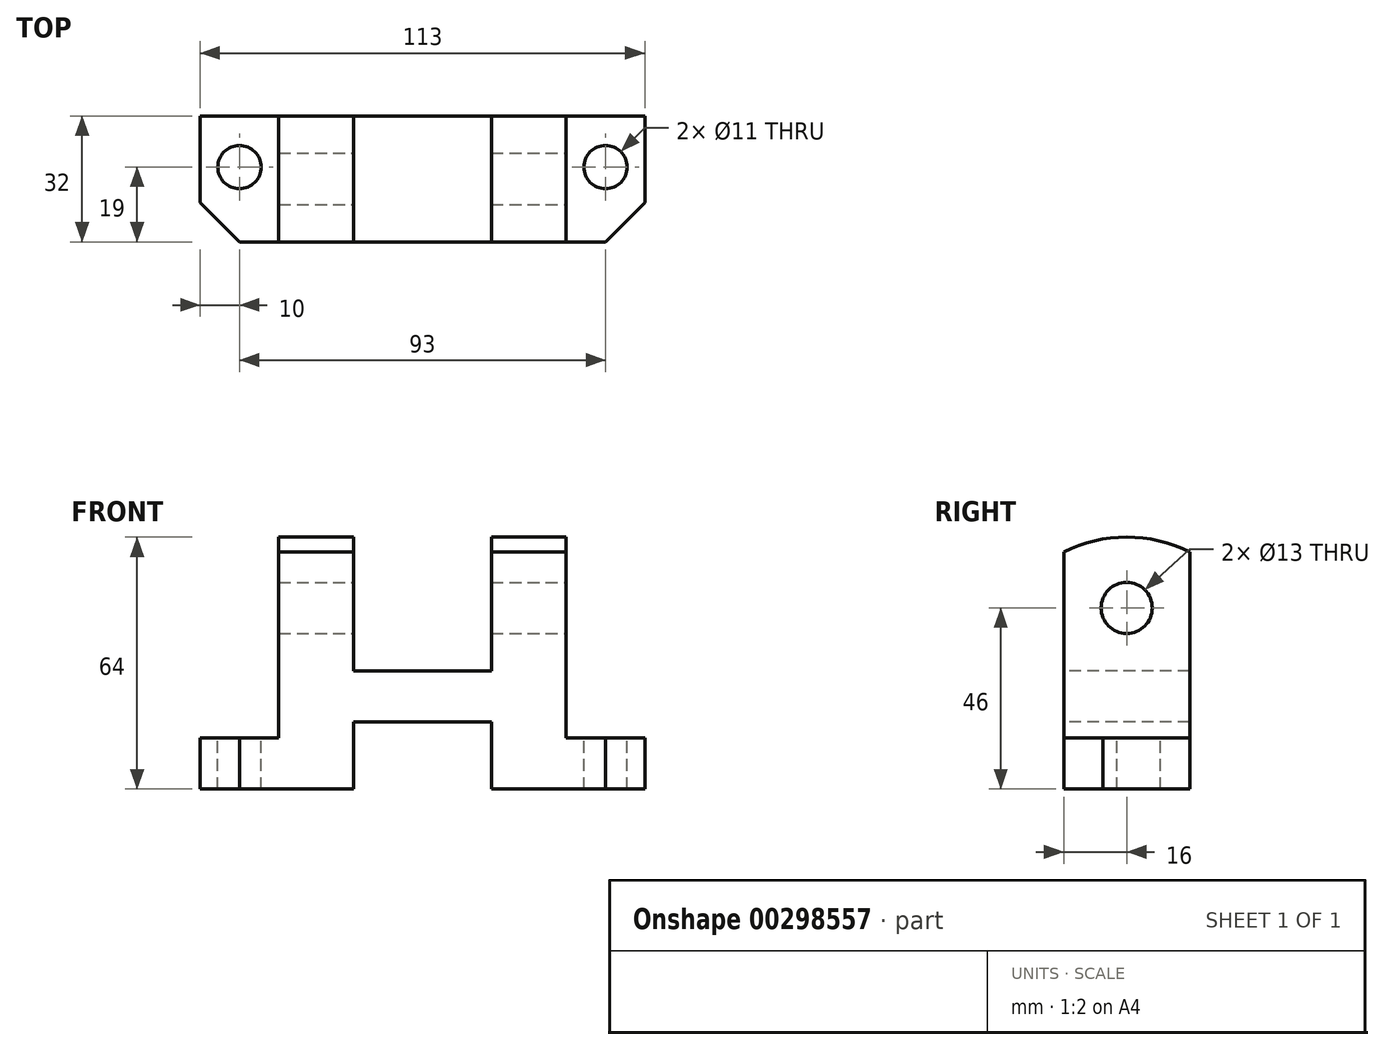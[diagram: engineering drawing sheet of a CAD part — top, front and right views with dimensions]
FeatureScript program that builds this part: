
annotation { "Feature Type Name" : "Feature", "Feature Type Description" : "" }
export const myFeature = defineFeature(function(context is Context, id is Id, definition is map)
    precondition{}
    {
        {
            var Q0;
            Q0=qCreatedBy(makeId("Front.planeOp"),FACE);
            var sketch = newSketch(context, id + "F0", { "sketchPlane" : qUnion([Q0])});
            skLineSegment(sketch, "E0.bottom", {"start": v(0, 0) * mm, "end": v(113, 0) * mm});
            skLineSegment(sketch, "E0.top", {"start": v(0, 64) * mm, "end": v(113, 64) * mm});
            skLineSegment(sketch, "E0.left", {"start": v(0, 0) * mm, "end": v(0, 64) * mm});
            skLineSegment(sketch, "E0.right", {"start": v(113, 0) * mm, "end": v(113, 64) * mm});
            skSolve(sketch);
        }
        {
            var Q0;
            Q0 = qSketchRegion(id + "F0", true);
            extrude(context, id + "F1", {"entities" : qUnion([Q0]), "depth" : 32 * mm});
        }
        {
            var Q0;
            Q0=makeQuery(id+"F1.opExtrude","CAP_FACE",FACE,{"disambiguationData":[OSD([sQuery(id+"F0.wireOp",EDGE,"E0.bottom"),sQuery(id+"F0.wireOp",EDGE,"E0.top"),sQuery(id+"F0.wireOp",EDGE,"E0.left"),sQuery(id+"F0.wireOp",EDGE,"E0.right")])],"isStart":false});
            var sketch = newSketch(context, id + "F2", { "sketchPlane" : qUnion([Q0])});
            skLineSegment(sketch, "E1.bottom", {"start": v(39, 0) * mm, "end": v(74, 0) * mm});
            skLineSegment(sketch, "E1.top", {"start": v(39, 17) * mm, "end": v(74, 17) * mm});
            skLineSegment(sketch, "E1.left", {"start": v(39, 0) * mm, "end": v(39, 17) * mm});
            skLineSegment(sketch, "E1.right", {"start": v(74, 0) * mm, "end": v(74, 17) * mm});
            skLineSegment(sketch, "E2.bottom", {"start": v(39, 64) * mm, "end": v(74, 64) * mm});
            skLineSegment(sketch, "E2.top", {"start": v(39, 30) * mm, "end": v(74, 30) * mm});
            skLineSegment(sketch, "E2.left", {"start": v(39, 64) * mm, "end": v(39, 30) * mm});
            skLineSegment(sketch, "E2.right", {"start": v(74, 64) * mm, "end": v(74, 30) * mm});
            skLineSegment(sketch, "E3.bottom", {"start": v(0, 64) * mm, "end": v(20, 64) * mm});
            skLineSegment(sketch, "E3.top", {"start": v(0, 13) * mm, "end": v(20, 13) * mm});
            skLineSegment(sketch, "E3.left", {"start": v(0, 64) * mm, "end": v(0, 13) * mm});
            skLineSegment(sketch, "E3.right", {"start": v(20, 64) * mm, "end": v(20, 13) * mm});
            skLineSegment(sketch, "E4.bottom", {"start": v(113, 64) * mm, "end": v(93, 64) * mm});
            skLineSegment(sketch, "E4.top", {"start": v(113, 13) * mm, "end": v(93, 13) * mm});
            skLineSegment(sketch, "E4.left", {"start": v(113, 64) * mm, "end": v(113, 13) * mm});
            skLineSegment(sketch, "E4.right", {"start": v(93, 64) * mm, "end": v(93, 13) * mm});
            skSolve(sketch);
        }
        {
            var Q0;
            Q0=makeQuery(id+"F2.imprint","IMPRINT",FACE,{"disambiguationData":[TD([[makeQuery(id+"F2.imprint","IMPRINT",EDGE,{"derivedFrom":sQuery(id+"F2.wireOp",EDGE,"E3.bottom")}),-1.0]])]});
            var Q1;
            Q1=makeQuery(id+"F2.imprint","IMPRINT",FACE,{"disambiguationData":[TD([[makeQuery(id+"F2.imprint","IMPRINT",EDGE,{"derivedFrom":sQuery(id+"F2.wireOp",EDGE,"E2.bottom")}),-1.0]])]});
            var Q2;
            Q2=makeQuery(id+"F2.imprint","IMPRINT",FACE,{"disambiguationData":[TD([[makeQuery(id+"F2.imprint","IMPRINT",EDGE,{"derivedFrom":sQuery(id+"F2.wireOp",EDGE,"E1.bottom")}),1.0]])]});
            var Q3;
            Q3=makeQuery(id+"F2.imprint","IMPRINT",FACE,{"disambiguationData":[TD([[makeQuery(id+"F2.imprint","IMPRINT",EDGE,{"derivedFrom":sQuery(id+"F2.wireOp",EDGE,"E4.bottom")}),-1.0]])]});
            extrude(context, id + "F3", {"entities" : qUnion([Q0, Q1, Q2, Q3]), "operationType" : NewBodyOperationType.REMOVE, "endBound" : BoundingType.THROUGH_ALL, "oppositeDirection" : true, "depth" : 25 * mm});
        }
        {
            var Q0;
            Q0=makeQuery(id+"F3.boolean.opBoolean","COPY",FACE,{"derivedFrom":makeQuery(id+"F3.opExtrude","SWEPT_FACE",FACE,{"disambiguationData":[OSD([sQuery(id+"F2.wireOp",EDGE,"E4.top")])]})});
            var sketch = newSketch(context, id + "F4", { "sketchPlane" : qUnion([Q0])});
            skLineSegment(sketch, "E5", {"start": v(113, -32) * mm, "end": v(103, -32) * mm});
            skLineSegment(sketch, "E6", {"start": v(113, -32) * mm, "end": v(113, -22) * mm});
            skLineSegment(sketch, "E7", {"start": v(113, -22) * mm, "end": v(103, -32) * mm});
            skLineSegment(sketch, "E8", {"start": v(0, -32) * mm, "end": v(10, -32) * mm});
            skLineSegment(sketch, "E9", {"start": v(10, -32) * mm, "end": v(0, -22) * mm});
            skLineSegment(sketch, "E10", {"start": v(0, -22) * mm, "end": v(0, -32) * mm});
            skSolve(sketch);
        }
        {
            var Q0;
            Q0 = qSketchRegion(id + "F4", true);
            extrude(context, id + "F5", {"entities" : qUnion([Q0]), "operationType" : NewBodyOperationType.REMOVE, "oppositeDirection" : true, "depth" : 25 * mm});
        }
        {
            var Q0;
            Q0=makeQuery(id+"F3.boolean.opBoolean","COPY",FACE,{"derivedFrom":makeQuery(id+"F3.opExtrude","SWEPT_FACE",FACE,{"disambiguationData":[OSD([sQuery(id+"F2.wireOp",EDGE,"E4.right")])]})});
            var sketch = newSketch(context, id + "F6", { "sketchPlane" : qUnion([Q0])});
            skArc(sketch, "E11", {"start": v(0, 60.25) * mm, "mid": v(-16, 64) * mm, "end": v(-32, 60.25) * mm});
            skSolve(sketch);
        }
        {
            var Q0;
            {var subQ0=sQuery(id+"F6.wireOp",EDGE,"E11");var subQ1=sQuery(id+"F2.wireOp",EDGE,"E4.right");var subQ2=makeQuery(id+"F3.boolean.opBoolean","COPY",EDGE,{"derivedFrom":makeQuery(id+"F3.opExtrude","CAP_EDGE",EDGE,{"disambiguationData":[OSD([subQ1])],"isStart":true})});var subQ3=makeQuery(id+"F6.imprint","INTERSECT",VERTEX,{"derivedFrom":[subQ2,subQ0]});Q0=makeQuery(id+"F6.imprint","IMPRINT",FACE,{"disambiguationData":[TD([[makeQuery(id+"F6.imprint","IMPRINT",EDGE,{"disambiguationData":[TD([[subQ3,1.0]])],"derivedFrom":subQ0}),-1.0]])]});}
            var Q1;
            {var subQ0=sQuery(id+"F6.wireOp",EDGE,"E11");var subQ1=sQuery(id+"F2.wireOp",EDGE,"E4.right");var subQ2=sQuery(id+"F0.wireOp",EDGE,"E0.top");var subQ5=makeQuery(id+"F3.boolean.opBoolean","COPY",EDGE,{"derivedFrom":makeQuery(id+"F3.opExtrude","SWEPT_EDGE",EDGE,{"disambiguationData":[OSD([subQ2,sQuery(id+"F2.wireOp",EDGE,"E4.bottom"),subQ1])]})});var subQ6=makeQuery(id+"F6.imprint","INTERSECT",VERTEX,{"derivedFrom":[subQ5,subQ0]});Q1=makeQuery(id+"F6.imprint","IMPRINT",FACE,{"disambiguationData":[TD([[makeQuery(id+"F6.imprint","IMPRINT",EDGE,{"disambiguationData":[TD([[subQ6,1.0]])],"derivedFrom":subQ0}),-1.0]])]});}
            extrude(context, id + "F7", {"entities" : qUnion([Q0, Q1]), "operationType" : NewBodyOperationType.REMOVE, "endBound" : BoundingType.THROUGH_ALL, "oppositeDirection" : true, "depth" : 25 * mm});
        }
        {
            var Q0;
            Q0=makeQuery(id+"F3.boolean.opBoolean","COPY",FACE,{"derivedFrom":makeQuery(id+"F3.opExtrude","SWEPT_FACE",FACE,{"disambiguationData":[OSD([sQuery(id+"F2.wireOp",EDGE,"E4.right")])]})});
            var sketch = newSketch(context, id + "F8", { "sketchPlane" : qUnion([Q0])});
            skCircle(sketch, "E12", {"center": v(-16, 46) * mm, "radius": 6.5 * mm});
            skSolve(sketch);
        }
        {
            var Q0;
            Q0 = qSketchRegion(id + "F8", true);
            extrude(context, id + "F9", {"entities" : qUnion([Q0]), "operationType" : NewBodyOperationType.REMOVE, "endBound" : BoundingType.THROUGH_ALL, "oppositeDirection" : true, "depth" : 25 * mm});
        }
        {
            var Q0;
            Q0=makeQuery(id+"F3.boolean.opBoolean","COPY",FACE,{"derivedFrom":makeQuery(id+"F3.opExtrude","SWEPT_FACE",FACE,{"disambiguationData":[OSD([sQuery(id+"F2.wireOp",EDGE,"E3.top")])]})});
            var sketch = newSketch(context, id + "F10", { "sketchPlane" : qUnion([Q0])});
            skCircle(sketch, "E13", {"center": v(10, -13) * mm, "radius": 5.5 * mm});
            skSolve(sketch);
        }
        {
            var Q0;
            Q0=makeQuery(id+"F3.boolean.opBoolean","COPY",FACE,{"derivedFrom":makeQuery(id+"F3.opExtrude","SWEPT_FACE",FACE,{"disambiguationData":[OSD([sQuery(id+"F2.wireOp",EDGE,"E4.top")])]})});
            var sketch = newSketch(context, id + "F11", { "sketchPlane" : qUnion([Q0])});
            skCircle(sketch, "E14", {"center": v(103, -13) * mm, "radius": 5.5 * mm});
            skSolve(sketch);
        }
        {
            var Q0;
            Q0 = qSketchRegion(id + "F11", true);
            var Q1;
            Q1=makeQuery(id+"F10.imprint","IMPRINT",FACE,{"disambiguationData":[TD([[makeQuery(id+"F10.imprint","IMPRINT",EDGE,{"derivedFrom":sQuery(id+"F10.wireOp",EDGE,"E13")}),1.0]])]});
            extrude(context, id + "F12", {"entities" : qUnion([Q0, Q1]), "operationType" : NewBodyOperationType.REMOVE, "endBound" : BoundingType.THROUGH_ALL, "oppositeDirection" : true, "depth" : 25 * mm});
        }
    });
